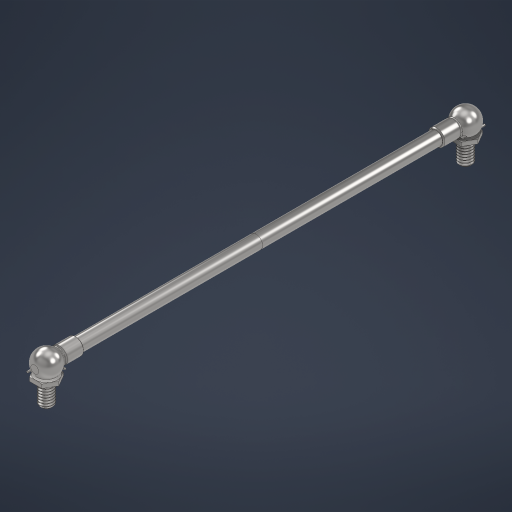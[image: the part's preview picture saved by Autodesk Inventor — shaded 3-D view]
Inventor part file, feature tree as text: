
AUTODESK INVENTOR PART (.ipt)
format: ipt  version: 2024 (Build 280153000, 153)  size: 1,313,280 bytes
history: native  units: in
note: dims shown in document units (in); Inventor stores cm internally (conversion verified against a paired STEP export)
features: other x7, revolve x2, extrude x1, sketch x1, fillet x1, sweep x1, pattern_circular x1
ambient origin geometry x8: Origin, YZ Plane, XZ Plane, XY Plane, X Axis, Y Axis, Z Axis, Center Point
bodies: Solid1 (feature_tree), Solid2 (feature_tree), Solid3 (feature_tree), Solid4 (feature_tree), Solid5 (feature_tree), Solid6 (feature_tree), Solid7 (feature_tree), Solid8 (feature_tree), Solid9 (feature_tree), Solid10 (feature_tree), Solid11 (feature_tree), Solid12 (feature_tree)
feature tree (14):
  other  "Cut-Extrude2"
  other  "Boss-Extrude2[1]"
  extrude  "Extrusion1"  Depth=0.5in
  sketch  "Sketch1"  dims[d0=1.0in d1=0.0in d2=0.5in d3=1.9685in]
  fillet  "Fillet1"  Radius=1.9685in
  revolve  "Revolve2[1]"  [1 undecoded]
  revolve  "Revolve2[2]"  [1 undecoded]
  sweep  "Sweep3"
  other  "CirPattern2[1]"
  other  "CirPattern2[3]"
  other  "Split1[3]"
  other  "Split1[4]"
  pattern_circular  "CirPattern6"
  other  "Boss-Extrude2[2]"
note: 2 required parameter values undecoded (feature->parameter linkage not recoverable at this tier; creation-order binding heuristic only, values carry confidence <= 0.55)
